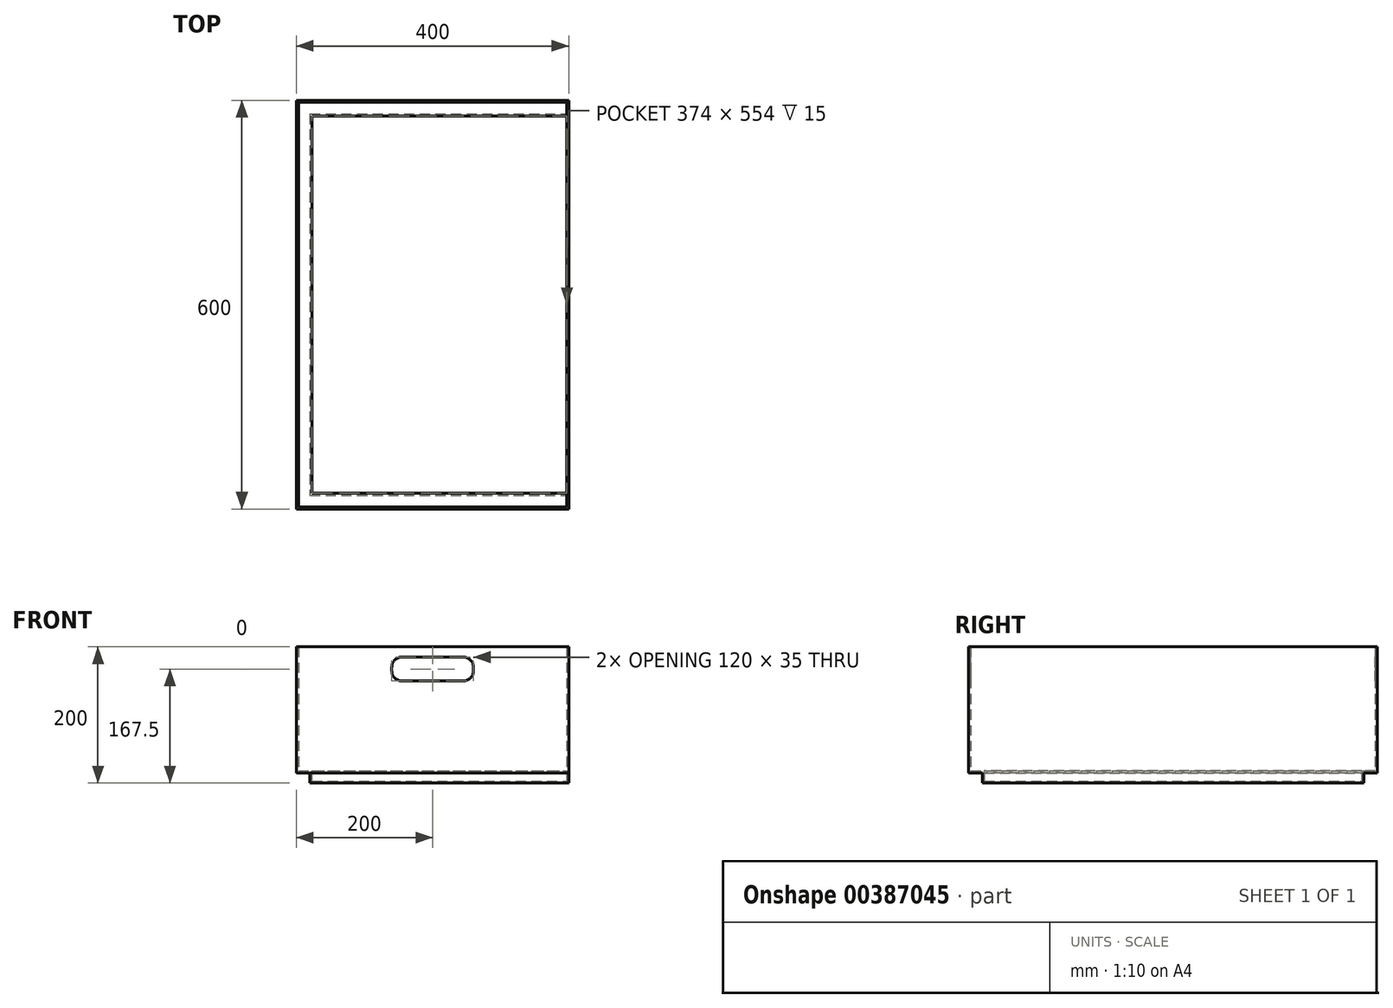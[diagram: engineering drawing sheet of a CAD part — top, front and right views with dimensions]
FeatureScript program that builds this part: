
annotation { "Feature Type Name" : "Feature", "Feature Type Description" : "" }
export const myFeature = defineFeature(function(context is Context, id is Id, definition is map)
    precondition{}
    {
        {
            var Q0;
            Q0=qCreatedBy(makeId("Front.planeOp"),FACE);
            var sketch = newSketch(context, id + "F0", { "sketchPlane" : qUnion([Q0])});
            skLineSegment(sketch, "E0.bottom", {"start": v(-200, 200) * mm, "end": v(200, 200) * mm});
            skLineSegment(sketch, "E0.top", {"start": v(-200, 0) * mm, "end": v(200, 0) * mm});
            skLineSegment(sketch, "E0.left", {"start": v(-200, 200) * mm, "end": v(-200, 0) * mm});
            skLineSegment(sketch, "E0.right", {"start": v(200, 200) * mm, "end": v(200, 0) * mm});
            skSolve(sketch);
        }
        {
            var Q0;
            Q0 = qSketchRegion(id + "F0", true);
            extrude(context, id + "F1", {"entities" : qUnion([Q0]), "endBound" : BoundingType.SYMMETRIC, "depth" : 600 * mm});
        }
        {
            var Q0;
            Q0=makeQuery(id+"F1.opExtrude","CAP_FACE",FACE,{"disambiguationData":[OSD([sQuery(id+"F0.wireOp",EDGE,"E0.bottom"),sQuery(id+"F0.wireOp",EDGE,"E0.top"),sQuery(id+"F0.wireOp",EDGE,"E0.left"),sQuery(id+"F0.wireOp",EDGE,"E0.right")])],"isStart":false});
            var sketch = newSketch(context, id + "F2", { "sketchPlane" : qUnion([Q0])});
            skLineSegment(sketch, "E1.bottom", {"start": v(-214.65, 15) * mm, "end": v(-180, 15) * mm});
            skLineSegment(sketch, "E1.top", {"start": v(-214.65, -26.77) * mm, "end": v(-180, -26.77) * mm});
            skLineSegment(sketch, "E1.left", {"start": v(-214.65, 15) * mm, "end": v(-214.65, -26.77) * mm});
            skLineSegment(sketch, "E1.right", {"start": v(-180, 15) * mm, "end": v(-180, -26.77) * mm});
            skSolve(sketch);
        }
        {
            var Q0;
            Q0 = qSketchRegion(id + "F2", true);
            extrude(context, id + "F3", {"entities" : qUnion([Q0]), "operationType" : NewBodyOperationType.REMOVE, "endBound" : BoundingType.THROUGH_ALL, "oppositeDirection" : true, "depth" : 25 * mm});
        }
        {
            var Q0;
            Q0=makeQuery(id+"F1.opExtrude","SWEPT_FACE",FACE,{"disambiguationData":[OSD([sQuery(id+"F0.wireOp",EDGE,"E0.right")])]});
            var sketch = newSketch(context, id + "F4", { "sketchPlane" : qUnion([Q0])});
            skLineSegment(sketch, "E2.bottom", {"start": v(-312.94, 15) * mm, "end": v(-280, 15) * mm});
            skLineSegment(sketch, "E2.top", {"start": v(-312.94, -8.16) * mm, "end": v(-280, -8.16) * mm});
            skLineSegment(sketch, "E2.left", {"start": v(-312.94, 15) * mm, "end": v(-312.94, -8.16) * mm});
            skLineSegment(sketch, "E2.right", {"start": v(-280, 15) * mm, "end": v(-280, -8.16) * mm});
            skLineSegment(sketch, "E3.MirrorCS", {"start": v(280, 15) * mm, "end": v(280, -8.16) * mm});
            skLineSegment(sketch, "E4.MirrorCS", {"start": v(312.94, 15) * mm, "end": v(312.94, -8.16) * mm});
            skLineSegment(sketch, "E5.MirrorCS", {"start": v(312.94, -8.16) * mm, "end": v(280, -8.16) * mm});
            skLineSegment(sketch, "E6.MirrorCS", {"start": v(312.94, 15) * mm, "end": v(280, 15) * mm});
            skSolve(sketch);
        }
        {
            var Q0;
            Q0 = qSketchRegion(id + "F4", true);
            extrude(context, id + "F5", {"entities" : qUnion([Q0]), "operationType" : NewBodyOperationType.REMOVE, "endBound" : BoundingType.THROUGH_ALL, "oppositeDirection" : true, "depth" : 25 * mm});
        }
        {
            var Q0;
            Q0=makeQuery(id+"F1.opExtrude","SWEPT_FACE",FACE,{"disambiguationData":[OSD([sQuery(id+"F0.wireOp",EDGE,"E0.bottom")])]});
            shell(context, id + "F6", {"entities" : qUnion([Q0]), "thickness" : 3 * mm});
        }
        {
            var Q0;
            Q0=makeQuery(id+"F1.opExtrude","CAP_FACE",FACE,{"disambiguationData":[OSD([sQuery(id+"F0.wireOp",EDGE,"E0.bottom"),sQuery(id+"F0.wireOp",EDGE,"E0.top"),sQuery(id+"F0.wireOp",EDGE,"E0.left"),sQuery(id+"F0.wireOp",EDGE,"E0.right")])],"isStart":false});
            var sketch = newSketch(context, id + "F7", { "sketchPlane" : qUnion([Q0])});
            skLineSegment(sketch, "E7.bottom", {"start": v(-45, 185) * mm, "end": v(45, 185) * mm});
            skLineSegment(sketch, "E7.top", {"start": v(-45, 150) * mm, "end": v(45, 150) * mm});
            skLineSegment(sketch, "E7.left", {"start": v(-60, 170) * mm, "end": v(-60, 165) * mm});
            skLineSegment(sketch, "E7.right", {"start": v(60, 170) * mm, "end": v(60, 165) * mm});
            skPoint(sketch, "E8.visualSharp", {"position": v(-60, 185) * mm});
            skArc(sketch, "E8.filletArc", {"start": v(-45, 185) * mm, "mid": v(-55.6, 180.6) * mm, "end": v(-60, 170) * mm});
            skPoint(sketch, "E9.visualSharp", {"position": v(60, 150) * mm});
            skArc(sketch, "E9.filletArc", {"start": v(45, 150) * mm, "mid": v(55.6, 154.4) * mm, "end": v(60, 165) * mm});
            skPoint(sketch, "E10.visualSharp", {"position": v(60, 185) * mm});
            skArc(sketch, "E10.filletArc", {"start": v(60, 170) * mm, "mid": v(55.6, 180.6) * mm, "end": v(45, 185) * mm});
            skPoint(sketch, "E11.visualSharp", {"position": v(-60, 150) * mm});
            skArc(sketch, "E11.filletArc", {"start": v(-60, 165) * mm, "mid": v(-55.6, 154.4) * mm, "end": v(-45, 150) * mm});
            skSolve(sketch);
        }
        {
            var Q0;
            Q0 = qSketchRegion(id + "F7", true);
            extrude(context, id + "F8", {"entities" : qUnion([Q0]), "operationType" : NewBodyOperationType.REMOVE, "endBound" : BoundingType.THROUGH_ALL, "oppositeDirection" : true, "depth" : 25 * mm});
        }
    });
